FCSTD DOCUMENT  (FreeCAD 0.22R37645 (Git))
Label: electronics cover panel
License: All rights reserved
LicenseURL: http://en.wikipedia.org/wiki/All_rights_reserved
objects: Sketcher::SketchObject×1
note: 1 computed .brp shape members not serialized (recipe doc carries the construction recipe); baked Part::Feature solids carry a one-line shape summary decoded from their .brp

FEATURE [Sketcher::SketchObject] Sketch
  FullyConstrained = true
  sketch-geometry (29):
    g0: LineSegment StartX=40 StartY=448 StartZ=0 EndX=130 EndY=448 EndZ=0
    g1: LineSegment StartX=280 StartY=448 StartZ=0 EndX=440 EndY=448 EndZ=0
    g2: GeomPoint X=30 Y=448 Z=0
    g3: LineSegment StartX=200 StartY=448 StartZ=0 EndX=200 EndY=438 EndZ=0
    g4: LineSegment StartX=200 StartY=438 StartZ=0 EndX=215 EndY=438 EndZ=0
    g5: LineSegment StartX=215 StartY=438 StartZ=0 EndX=215 EndY=398 EndZ=0
    g6: LineSegment StartX=270 StartY=398 StartZ=0 EndX=270 EndY=438 EndZ=0
    g7: LineSegment StartX=270 StartY=438 StartZ=0 EndX=280 EndY=438 EndZ=0
    g8: LineSegment StartX=280 StartY=438 StartZ=0 EndX=280 EndY=448 EndZ=0
    g9: LineSegment StartX=130 StartY=448 StartZ=0 EndX=130 EndY=438 EndZ=0
    g10: LineSegment StartX=130 StartY=438 StartZ=0 EndX=170 EndY=438 EndZ=0
    g11: LineSegment StartX=170 StartY=438 StartZ=0 EndX=170 EndY=448 EndZ=0
    g12: LineSegment StartX=170 StartY=448 StartZ=0 EndX=200 EndY=448 EndZ=0
    g13: GeomPoint X=450 Y=448 Z=0
    g14: LineSegment StartX=243.5 StartY=398 StartZ=0 EndX=270 EndY=398 EndZ=0
    g15: LineSegment StartX=241.5 StartY=398 StartZ=0 EndX=215 EndY=398 EndZ=0
    g16: GeomPoint X=242.5 Y=398 Z=0
    g17: ArcOfCircle CenterX=30 CenterY=448 CenterZ=0 NormalX=0 NormalY=0 NormalZ=1 AngleXU=0 Radius=10 StartAngle=4.71239 EndAngle=6.28319
    g18: ArcOfCircle CenterX=450 CenterY=448 CenterZ=0 NormalX=0 NormalY=0 NormalZ=1 AngleXU=0 Radius=10 StartAngle=3.14159 EndAngle=4.71239
    g19: LineSegment StartX=241.5 StartY=30 StartZ=0 EndX=80 EndY=30 EndZ=0
    g20: LineSegment StartX=80 StartY=30 StartZ=0 EndX=80 EndY=80 EndZ=0
    g21: LineSegment StartX=80 StartY=80 StartZ=0 EndX=30 EndY=80 EndZ=0
    g22: LineSegment StartX=243.5 StartY=30 StartZ=0 EndX=400 EndY=30 EndZ=0
    g23: LineSegment StartX=400 StartY=30 StartZ=0 EndX=400 EndY=80 EndZ=0
    g24: LineSegment StartX=400 StartY=80 StartZ=0 EndX=450 EndY=80 EndZ=0
    g25: LineSegment StartX=30 StartY=438 StartZ=0 EndX=30 EndY=80 EndZ=0
    g26: LineSegment StartX=450 StartY=438 StartZ=0 EndX=450 EndY=80 EndZ=0
    g27: LineSegment StartX=243.5 StartY=398 StartZ=0 EndX=243.5 EndY=30 EndZ=0
    g28: LineSegment StartX=241.5 StartY=30 StartZ=0 EndX=241.5 EndY=398 EndZ=0
  constraints (85):
    c: Horizontal(g0)
    c: Horizontal(g1)
    c: PointOnObject(g2,g0)
    c: DistanceX(g2,g12) = 170
    c: Horizontal(g1,g12)
    c: Coincident(g12,g3)
    c: Vertical(g3)
    c: Coincident(g3,g4)
    c: Coincident(g4,g5)
    c: Vertical(g5)
    c: Vertical(g6)
    c: Coincident(g6,g7)
    c: Horizontal(g7)
    c: Coincident(g7,g8)
    c: Coincident(g8,g1)
    c: Vertical(g8)
    c: Horizontal(g4)
    c: Horizontal(g4,g6)
    c: DistanceX(g17,g4) = 185
    c: DistanceY(g5,g12) = 50
    c: DistanceX(g2,g1) = 250
    c: Coincident(g9,g10)
    c: Horizontal(g10)
    c: Coincident(g10,g11)
    c: Vertical(g11)
    c: DistanceX(g2,g9) = 100
    c: DistanceX(g2,g11) = 140
    c: Vertical(g9)
    c: DistanceY(g9,g9) = 10
    c: Coincident(g0,g9)
    c: Coincident(g12,g11)
    c: DistanceX(g2,g6) = 240
    c: DistanceX(g2,g13) = 420
    c: Horizontal(g12)
    c: Horizontal(g3,g10)
    c: Horizontal(g11,g0)
    c: PointOnObject(g13,g1)
    c: Coincident(g14,g6)
    c: Horizontal(g14)
    c: Coincident(g15,g5)
    c: Symmetric(g5,g6,g16)
    c: Symmetric(g14,g15,g16)
    c: Horizontal(g5,g6)
    c: Coincident(g17,g0)
    c: Perpendicular(g17,g0)
    c: Coincident(g18,g1)
    c: Horizontal(g19)
    c: Coincident(g19,g20)
    c: Vertical(g20)
    c: Coincident(g20,g21)
    c: Horizontal(g21)
    c: DistanceY(g20,g20) = 50
    c: DistanceX(g21,g21) = 50
    c: Horizontal(g22)
    c: Coincident(g22,g23)
    c: Vertical(g23)
    c: Coincident(g23,g24)
    c: Horizontal(g24)
    c: Equal(g21,g24)
    c: Equal(g20,g23)
    c: Horizontal(g22,g19)
    c: Radius(g18) = 10
    c: Equal(g18,g17)
    c: Perpendicular(g18,g1)
    c: DistanceY(g19,g17) = 418
    c: Coincident(g25,g17)
    c: Coincident(g25,g21)
    c: Vertical(g25)
    c: PointOnObject(g26,g18)
    c: Coincident(g26,g24)
    c: Vertical(g26)
    c: Coincident(g27,g14)
    c: Coincident(g27,g22)
    c: Vertical(g27)
    c: Coincident(g28,g19)
    c: Coincident(g28,g15)
    c: Vertical(g28)
    c: Perpendicular(g17,g25)
    c: Perpendicular(g18,g26)
    c: DistanceX(g17,g15) = 211.5
    c: DistanceX(g5,g6) = 55
    c: PointOnObject(g18,g26)
    c: DistanceX(g17,g18) = 420
    c: DistanceY(g-1,g19) = 30
    c: DistanceX(g-1,g21) = 30
